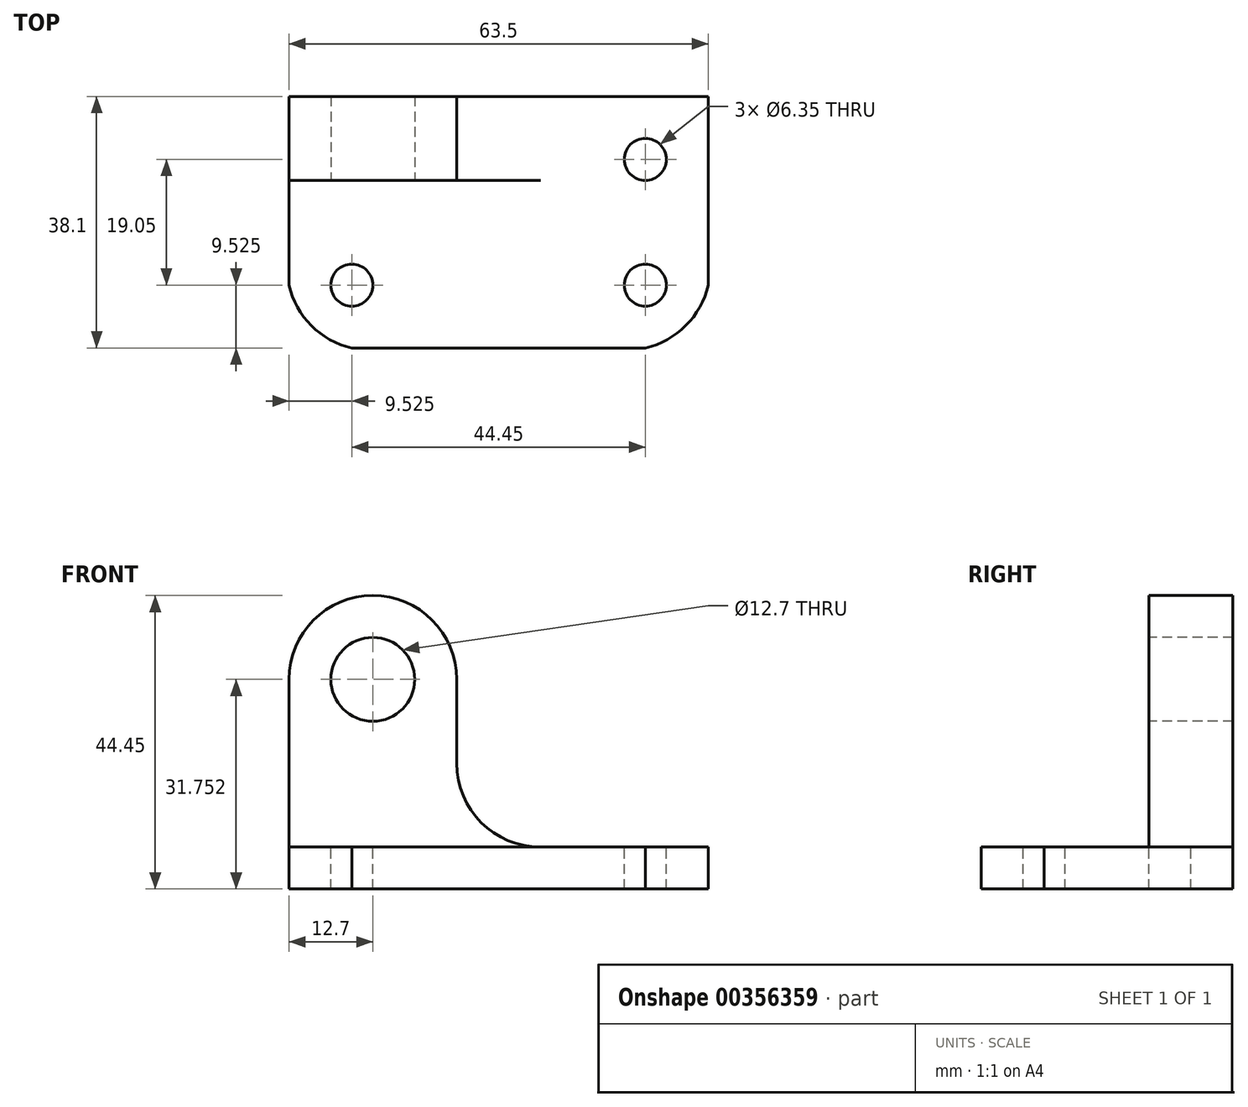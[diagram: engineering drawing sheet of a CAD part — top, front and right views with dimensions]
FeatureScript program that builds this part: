
annotation { "Feature Type Name" : "Feature", "Feature Type Description" : "" }
export const myFeature = defineFeature(function(context is Context, id is Id, definition is map)
    precondition{}
    {
        {
            var Q0;
            Q0=qCreatedBy(makeId("Front.planeOp"),FACE);
            var sketch = newSketch(context, id + "F0", { "sketchPlane" : qUnion([Q0])});
            skLineSegment(sketch, "E0.bottom", {"start": v(-35.57, 29.6) * mm, "end": v(27.93, 29.6) * mm});
            skLineSegment(sketch, "E0.top", {"start": v(-35.57, -14.86) * mm, "end": v(27.93, -14.86) * mm});
            skLineSegment(sketch, "E0.left", {"start": v(-35.57, 29.6) * mm, "end": v(-35.57, -14.86) * mm});
            skLineSegment(sketch, "E0.right", {"start": v(27.93, 29.6) * mm, "end": v(27.93, -14.86) * mm});
            skSolve(sketch);
        }
        {
            var Q0;
            Q0=makeQuery(id+"F0.imprint","IMPRINT",FACE,{"disambiguationData":[TD([[makeQuery(id+"F0.imprint","IMPRINT",EDGE,{"derivedFrom":sQuery(id+"F0.wireOp",EDGE,"E0.bottom")}),-1.0]])]});
            extrude(context, id + "F1", {"entities" : qUnion([Q0]), "depth" : 38.1 * mm});
        }
        {
            var Q0;
            Q0=makeQuery(id+"F1.opExtrude","CAP_FACE",FACE,{"disambiguationData":[OSD([sQuery(id+"F0.wireOp",EDGE,"E0.bottom"),sQuery(id+"F0.wireOp",EDGE,"E0.top"),sQuery(id+"F0.wireOp",EDGE,"E0.left"),sQuery(id+"F0.wireOp",EDGE,"E0.right")])],"isStart":false});
            var sketch = newSketch(context, id + "F2", { "sketchPlane" : qUnion([Q0])});
            skLineSegment(sketch, "E1", {"start": v(-35.57, -8.5) * mm, "end": v(27.93, -8.5) * mm});
            skSolve(sketch);
        }
        {
            var Q0;
            {var subQ0=sQuery(id+"F2.wireOp",EDGE,"E1");Q0=makeQuery(id+"F2.imprint","IMPRINT",FACE,{"disambiguationData":[TD([[makeQuery(id+"F2.imprint","IMPRINT",EDGE,{"derivedFrom":subQ0}),1.0]])]});}
            extrude(context, id + "F3", {"entities" : qUnion([Q0]), "operationType" : NewBodyOperationType.REMOVE, "oppositeDirection" : true, "depth" : 25.4 * mm});
        }
        {
            var Q0;
            Q0=makeQuery(id+"F3.boolean.opBoolean","COPY",FACE,{"derivedFrom":makeQuery(id+"F3.opExtrude","CAP_FACE",FACE,{"disambiguationData":[OSD([sQuery(id+"F0.wireOp",EDGE,"E0.bottom"),sQuery(id+"F0.wireOp",EDGE,"E0.left"),sQuery(id+"F0.wireOp",EDGE,"E0.right"),sQuery(id+"F2.wireOp",EDGE,"E1")])],"isStart":false})});
            var sketch = newSketch(context, id + "F4", { "sketchPlane" : qUnion([Q0])});
            skLineSegment(sketch, "E2", {"start": v(-35.57, -8.5) * mm, "end": v(-35.57, 16.9) * mm});
            skLineSegment(sketch, "E3", {"start": v(-22.87, 29.6) * mm, "end": v(-22.87, 29.6) * mm});
            skLineSegment(sketch, "E4", {"start": v(-10.17, 16.9) * mm, "end": v(-10.17, 4.2) * mm});
            skLineSegment(sketch, "E5", {"start": v(2.53, -8.5) * mm, "end": v(2.53, -8.5) * mm});
            skPoint(sketch, "E6.visualSharp", {"position": v(-35.57, 29.6) * mm});
            skArc(sketch, "E6.filletArc", {"start": v(-22.87, 29.6) * mm, "mid": v(-31.85, 25.87) * mm, "end": v(-35.57, 16.9) * mm});
            skPoint(sketch, "E7.visualSharp", {"position": v(-10.17, 29.6) * mm});
            skArc(sketch, "E7.filletArc", {"start": v(-10.17, 16.9) * mm, "mid": v(-13.89, 25.87) * mm, "end": v(-22.87, 29.6) * mm});
            skPoint(sketch, "E8.visualSharp", {"position": v(-10.17, -8.5) * mm});
            skArc(sketch, "E8.filletArc", {"start": v(-10.17, 4.2) * mm, "mid": v(-6.45, -4.79) * mm, "end": v(2.53, -8.5) * mm});
            skCircle(sketch, "E9", {"center": v(-22.87, 16.9) * mm, "radius": 6.35 * mm});
            skSolve(sketch);
        }
        {
            var Q0;
            {var subQ0=sQuery(id+"F4.wireOp",EDGE,"E6.filletArc");Q0=makeQuery(id+"F4.imprint","IMPRINT",FACE,{"disambiguationData":[TD([[makeQuery(id+"F4.imprint","IMPRINT",EDGE,{"derivedFrom":subQ0}),-1.0]])]});}
            var Q1;
            Q1=makeQuery(id+"F4.imprint","IMPRINT",FACE,{"disambiguationData":[TD([[makeQuery(id+"F4.imprint","IMPRINT",EDGE,{"derivedFrom":sQuery(id+"F4.wireOp",EDGE,"E4")}),1.0]])]});
            var Q2;
            Q2=makeQuery(id+"F4.imprint","IMPRINT",FACE,{"disambiguationData":[TD([[makeQuery(id+"F4.imprint","IMPRINT",EDGE,{"derivedFrom":sQuery(id+"F4.wireOp",EDGE,"E9")}),1.0]])]});
            extrude(context, id + "F5", {"entities" : qUnion([Q0, Q1, Q2]), "operationType" : NewBodyOperationType.REMOVE, "oppositeDirection" : true, "depth" : 12.7 * mm});
        }
        {
            var Q0;
            {var subQ0=sQuery(id+"F2.wireOp",EDGE,"E1");Q0=makeQuery(id+"F5.boolean.opBoolean","MERGE",FACE,{"derivedFrom":[makeQuery(id+"F3.boolean.opBoolean","COPY",FACE,{"derivedFrom":makeQuery(id+"F3.opExtrude","SWEPT_FACE",FACE,{"disambiguationData":[OSD([subQ0])]})}),makeQuery(id+"F5.opExtrude","SWEPT_FACE",FACE,{"disambiguationData":[OSD([subQ0])]})]});}
            var sketch = newSketch(context, id + "F6", { "sketchPlane" : qUnion([Q0])});
            skCircle(sketch, "E10", {"center": v(18.4, -9.52) * mm, "radius": 3.18 * mm});
            skCircle(sketch, "E11", {"center": v(18.4, -28.58) * mm, "radius": 3.18 * mm});
            skCircle(sketch, "E12", {"center": v(-26.04, -28.58) * mm, "radius": 3.18 * mm});
            skArc(sketch, "E13", {"start": v(18.4, -38.1) * mm, "mid": v(24.53, -34.7) * mm, "end": v(27.93, -28.57) * mm});
            skArc(sketch, "E14", {"start": v(-35.57, -28.58) * mm, "mid": v(-32.17, -34.7) * mm, "end": v(-26.04, -38.1) * mm});
            skSolve(sketch);
        }
        {
            var Q0;
            Q0=makeQuery(id+"F6.imprint","IMPRINT",FACE,{"disambiguationData":[TD([[makeQuery(id+"F6.imprint","IMPRINT",EDGE,{"derivedFrom":sQuery(id+"F6.wireOp",EDGE,"E10")}),1.0]])]});
            var Q1;
            Q1=makeQuery(id+"F6.imprint","IMPRINT",FACE,{"disambiguationData":[TD([[makeQuery(id+"F6.imprint","IMPRINT",EDGE,{"derivedFrom":sQuery(id+"F6.wireOp",EDGE,"E11")}),1.0]])]});
            var Q2;
            Q2=makeQuery(id+"F6.imprint","IMPRINT",FACE,{"disambiguationData":[TD([[makeQuery(id+"F6.imprint","IMPRINT",EDGE,{"derivedFrom":sQuery(id+"F6.wireOp",EDGE,"E12")}),1.0]])]});
            var Q3;
            {var subQ0=sQuery(id+"F6.wireOp",EDGE,"E14");Q3=makeQuery(id+"F6.imprint","IMPRINT",FACE,{"disambiguationData":[TD([[makeQuery(id+"F6.imprint","IMPRINT",EDGE,{"derivedFrom":subQ0}),-1.0]])]});}
            var Q4;
            {var subQ0=sQuery(id+"F6.wireOp",EDGE,"E13");Q4=makeQuery(id+"F6.imprint","IMPRINT",FACE,{"disambiguationData":[TD([[makeQuery(id+"F6.imprint","IMPRINT",EDGE,{"derivedFrom":subQ0}),-1.0]])]});}
            extrude(context, id + "F7", {"entities" : qUnion([Q0, Q1, Q2, Q3, Q4]), "operationType" : NewBodyOperationType.REMOVE, "oppositeDirection" : true, "depth" : 6.35 * mm});
        }
    });
